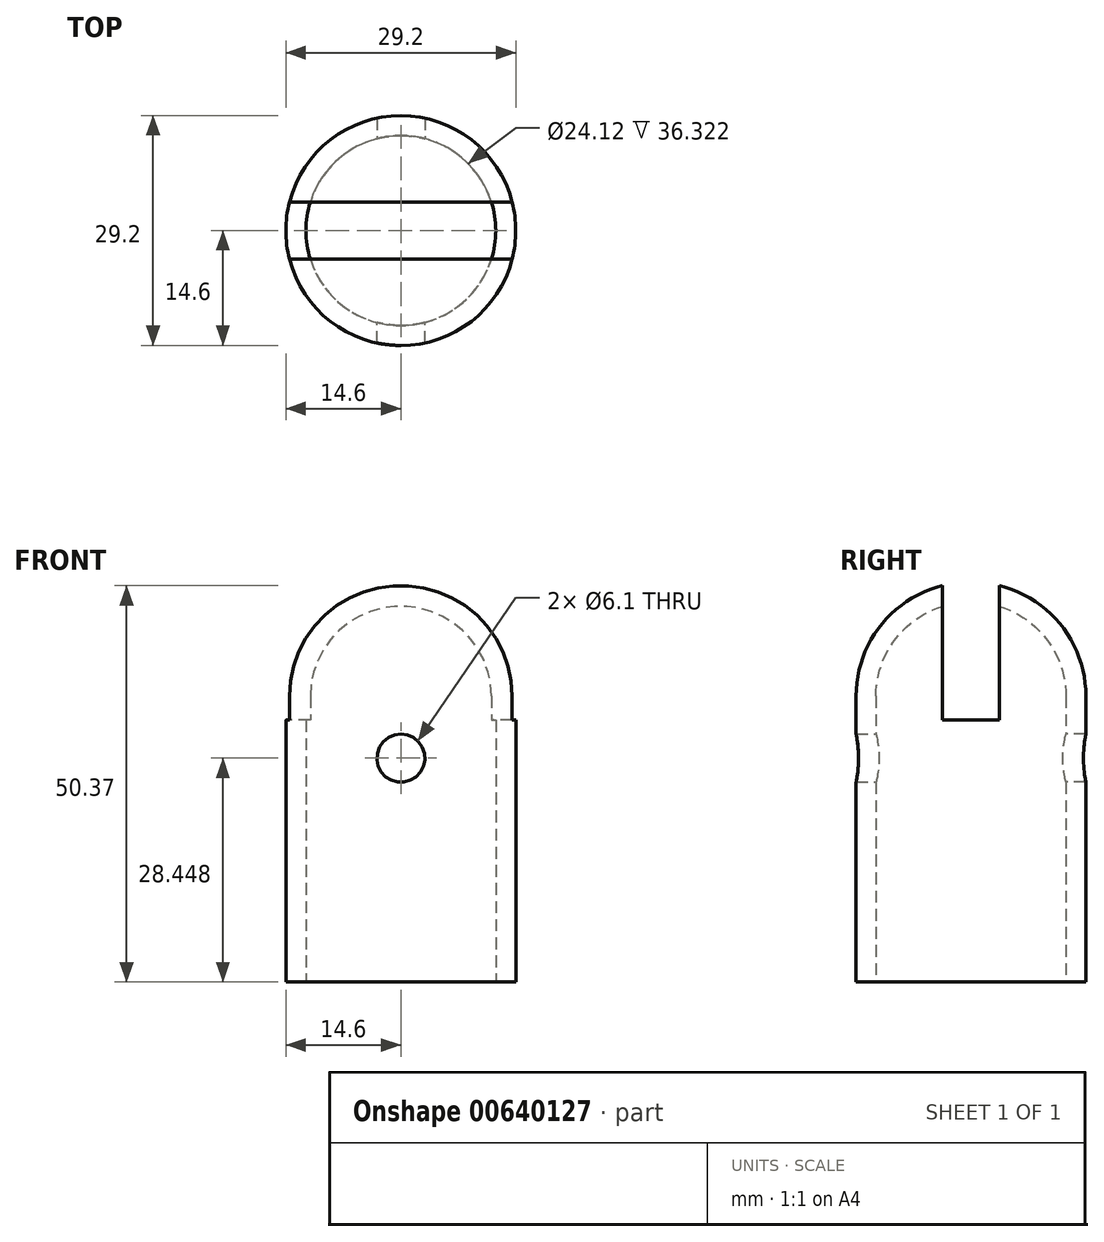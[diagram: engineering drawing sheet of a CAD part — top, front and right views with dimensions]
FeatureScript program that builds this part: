
annotation { "Feature Type Name" : "Feature", "Feature Type Description" : "" }
export const myFeature = defineFeature(function(context is Context, id is Id, definition is map)
    precondition{}
    {
        {
            var Q0;
            Q0=qCreatedBy(makeId("Top.planeOp"),FACE);
            var sketch = newSketch(context, id + "F0", { "sketchPlane" : qUnion([Q0])});
            skPoint(sketch, "E0.middle", {"position": v(0, 0) * mm});
            skCircle(sketch, "E1", {"center": v(0, 0) * mm, "radius": 14.6 * mm});
            skSolve(sketch);
        }
        {
            var Q0;
            Q0 = qSketchRegion(id + "F0", true);
            extrude(context, id + "F1", {"entities" : qUnion([Q0]), "depth" : 50.8 * mm, "offsetDistance" : 25.4 * mm});
        }
        {
            var Q0;
            Q0=makeQuery(id+"F1.opExtrude","CAP_EDGE",EDGE,{"disambiguationData":[OSD([sQuery(id+"F0.wireOp",EDGE,"E1")])],"isStart":false});
            var Q1;
            Q1=makeQuery(id+"F1.opExtrude","CAP_FACE",FACE,{"disambiguationData":[OSD([sQuery(id+"F0.wireOp",EDGE,"E1")])],"isStart":false});
            fillet(context, id + "F2", {"entities" : qUnion([Q0, Q1]), "radius" : 14.48 * mm, "tangentPropagation" : true, "allowEdgeOverflow" : false});
        }
        {
            var Q0;
            Q0=makeQuery(id+"F1.opExtrude","CAP_FACE",FACE,{"disambiguationData":[OSD([sQuery(id+"F0.wireOp",EDGE,"E1")])],"isStart":true});
            shell(context, id + "F3", {"entities" : qUnion([Q0]), "thickness" : 2.54 * mm});
        }
        {
            var Q0;
            Q0=makeQuery(id+"F1.opExtrude","CAP_FACE",FACE,{"disambiguationData":[OSD([sQuery(id+"F0.wireOp",EDGE,"E1")])],"isStart":false});
            var sketch = newSketch(context, id + "F4", { "sketchPlane" : qUnion([Q0])});
            skLineSegment(sketch, "E2.bottom", {"start": v(15.85, 3.63) * mm, "end": v(-15.85, 3.63) * mm});
            skLineSegment(sketch, "E2.top", {"start": v(15.85, -3.63) * mm, "end": v(-15.85, -3.63) * mm});
            skLineSegment(sketch, "E2.left", {"start": v(15.85, 3.63) * mm, "end": v(15.85, -3.63) * mm});
            skLineSegment(sketch, "E2.right", {"start": v(-15.85, 3.63) * mm, "end": v(-15.85, -3.63) * mm});
            skPoint(sketch, "E2.middle", {"position": v(0, 0) * mm});
            skSolve(sketch);
        }
        {
            var Q0;
            Q0=makeQuery(id+"F4.imprint","IMPRINT",FACE,{"disambiguationData":[TD([[makeQuery(id+"F4.imprint","IMPRINT",EDGE,{"derivedFrom":sQuery(id+"F4.wireOp",EDGE,"E2.bottom")}),1.0]])]});
            var Q1;
            Q1=makeQuery(id+"F1.opExtrude","CAP_FACE",FACE,{"disambiguationData":[OSD([sQuery(id+"F0.wireOp",EDGE,"E1")])],"isStart":false});
            var Q2;
            {var subQ0=sQuery(id+"F0.wireOp",EDGE,"E1");Q2=makeQuery(id+"F3.opShell","OFFSET_FACE",FACE,{"disambiguationData":[OSD([subQ0]),TDD([makeQuery(id+"F1.opExtrude","CAP_FACE",FACE,{"disambiguationData":[OSD([subQ0])],"isStart":false})])]});}
            extrude(context, id + "F5", {"entities" : qUnion([Q0, Q1, Q2]), "operationType" : NewBodyOperationType.REMOVE, "oppositeDirection" : true, "depth" : 17.53 * mm, "offsetDistance" : 25.4 * mm});
        }
        {
            var Q0;
            Q0=qCreatedBy(makeId("Front.planeOp"),FACE);
            var sketch = newSketch(context, id + "F6", { "sketchPlane" : qUnion([Q0])});
            skCircle(sketch, "E3", {"center": v(0, 28.45) * mm, "radius": 3.05 * mm});
            skSolve(sketch);
        }
        {
            var Q0;
            Q0 = qSketchRegion(id + "F6", true);
            extrude(context, id + "F7", {"entities" : qUnion([Q0]), "operationType" : NewBodyOperationType.REMOVE, "oppositeDirection" : true, "depth" : 23.88 * mm, "offsetDistance" : 25.4 * mm});
        }
        {
            var Q0;
            Q0=qCreatedBy(makeId("Front.planeOp"),FACE);
            var sketch = newSketch(context, id + "F8", { "sketchPlane" : qUnion([Q0])});
            skCircle(sketch, "E4", {"center": v(0, 28.45) * mm, "radius": 3.05 * mm});
            skSolve(sketch);
        }
        {
            var Q0;
            Q0=makeQuery(id+"F8.imprint","IMPRINT",FACE,{"disambiguationData":[TD([[makeQuery(id+"F8.imprint","IMPRINT",EDGE,{"derivedFrom":sQuery(id+"F8.wireOp",EDGE,"E4")}),1.0]])]});
            extrude(context, id + "F9", {"entities" : qUnion([Q0]), "operationType" : NewBodyOperationType.REMOVE, "depth" : 37.6 * mm, "offsetDistance" : 25.4 * mm});
        }
    });
